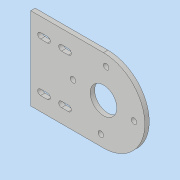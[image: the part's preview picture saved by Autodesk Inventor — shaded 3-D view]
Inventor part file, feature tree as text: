
AUTODESK INVENTOR PART (.ipt)
format: ipt  version: 2017 (Build 210142000, 142)  size: 149,504 bytes
history: native  units: in
note: dims shown in document units (in); Inventor stores cm internally (conversion verified against a paired STEP export)
features: sketch x1, extrude x1
ambient origin geometry x8: Origin, YZ Plane, XZ Plane, XY Plane, X Axis, Y Axis, Z Axis, Center Point
bodies: Solid1 (feature_tree)
feature tree (2):
  sketch  "Sketch1"  dims[d0=2.3228in d1=2.0472in d2=0.75in d3=0.1575in d4=0.1575in d5=0.1575in d6=0.1575in d7=2.4393in d8=1.2205in d9=1.2205in d10=1.2205in d11=2.6394in d13=0.159in d14=0.159in d16=0.159in d17=0.159in d18=0.159in d19=0.159in d20=0.159in d21=0.159in d22=0.1969in d23=0.1969in d24=0.1969in d25=0.1969in d26=0.159in d27=0.9843in d29=0.5906in d30=0.125in d31=0.0in d32=1.378in]
  extrude  "Extrusion1"  Depth=1.378in
